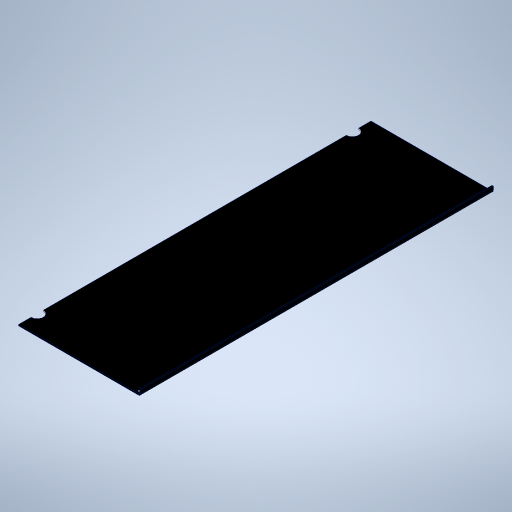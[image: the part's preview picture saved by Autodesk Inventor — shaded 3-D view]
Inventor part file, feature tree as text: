
AUTODESK INVENTOR PART (.ipt)
format: ipt  version: 2023 (Build 270158000, 158)  size: 292,352 bytes
history: native  units: in
note: dims shown in document units (in); Inventor stores cm internally (conversion verified against a paired STEP export)
features: sheet_metal_op x4, sketch x4, hole x2, other x2, pattern_linear x1
ambient origin geometry x8: Origin, YZ Plane, XZ Plane, XY Plane, X Axis, Y Axis, Z Axis, Center Point
bodies: Solid1 (feature_tree)
feature tree (13):
  sheet_metal_op  "Face1"
  sheet_metal_op  "Flange1"
  hole  "Hole1"  [1 undecoded]
  pattern_linear  "Rectangular Pattern1"  Spacing1=0.0875in  [1 undecoded]
  hole  "Hole2"  [1 undecoded]
  sketch  "Sketch1"  dims[d0=7.6378in d1=22.4409in]
  other  "Plate1"
  sketch  "Sketch3"  dims[d2=3.8189in]
  other  "Plate2"
  sheet_metal_op  "Bend1"
  sheet_metal_op  "Corner1"
  sketch  "Sketch4"  dims[d3=11.2205in]
  sketch  "Sketch5"  dims[d4=0.0875in d5=0.0875in d6=0.0438in d7=0.175in d8=0.0875in d9=0.3937in d10=90.0deg d11=0.0669in d12=0.35in d13=0.0875in d14=0.0875in d15=0.194in d16=0.2953in d17=0.1476in d18=0.0984in d19=90.0deg d20=0.0875in d21=0.8108in d22=0.1939in d23=2.7559in d25=3.6755in d27=0.162in d28=0.7874in d29=0.2953in d30=0.1476in d31=0.0984in d32=90.0deg d33=0.3937in d34=0.8108in d35=1.1811in d36=1.1811in]
note: 3 required parameter values undecoded (feature->parameter linkage not recoverable at this tier; creation-order binding heuristic only, values carry confidence <= 0.55)
